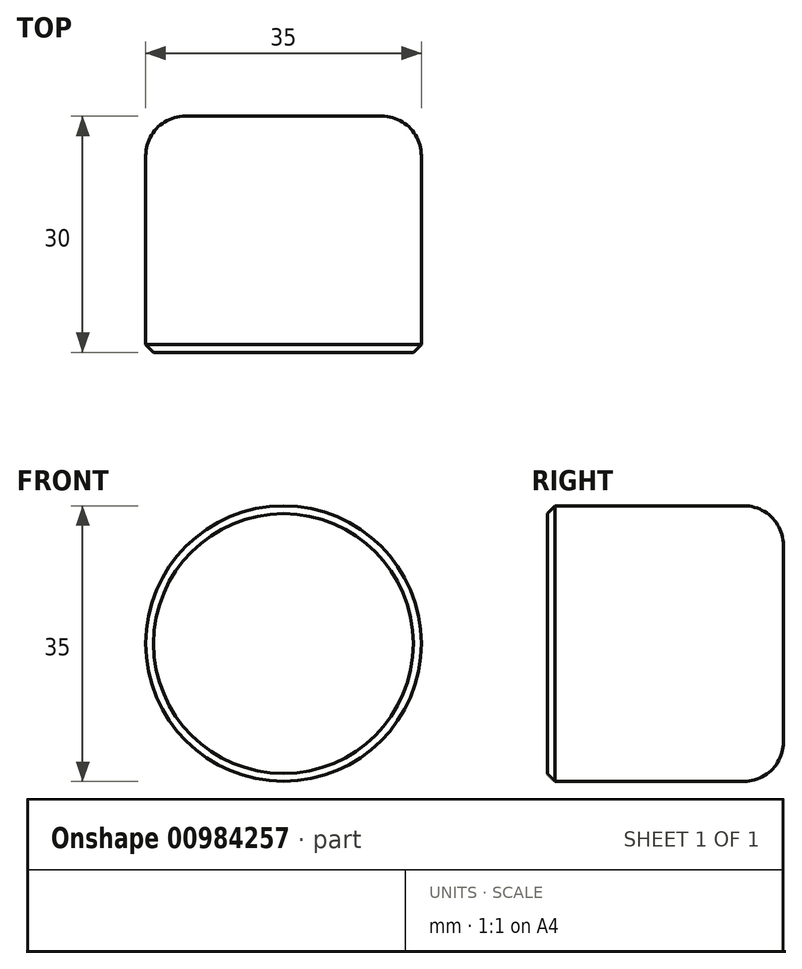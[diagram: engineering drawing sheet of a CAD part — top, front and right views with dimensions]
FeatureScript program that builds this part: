
annotation { "Feature Type Name" : "Feature", "Feature Type Description" : "" }
export const myFeature = defineFeature(function(context is Context, id is Id, definition is map)
    precondition{}
    {
        {
            var Q0;
            Q0=qCreatedBy(makeId("Front.planeOp"),FACE);
            var sketch = newSketch(context, id + "F0", { "sketchPlane" : qUnion([Q0])});
            skCircle(sketch, "E0", {"center": v(0, 0) * mm, "radius": 17.5 * mm});
            skSolve(sketch);
        }
        {
            var Q0;
            Q0=makeQuery(id+"F0.imprint","IMPRINT",FACE,{"disambiguationData":[TD([[makeQuery(id+"F0.imprint","IMPRINT",EDGE,{"derivedFrom":sQuery(id+"F0.wireOp",EDGE,"E0")}),1.0]])]});
            extrude(context, id + "F1", {"entities" : qUnion([Q0]), "depth" : 30 * mm, "offsetDistance" : 25 * mm});
        }
        {
            var Q0;
            Q0=makeQuery(id+"F1.opExtrude","CAP_EDGE",EDGE,{"disambiguationData":[OSD([sQuery(id+"F0.wireOp",EDGE,"E0")])],"isStart":true});
            fillet(context, id + "F2", {"entities" : qUnion([Q0]), "radius" : 5 * mm, "tangentPropagation" : true, "allowEdgeOverflow" : false});
        }
        {
            var Q0;
            Q0=makeQuery(id+"F1.opExtrude","CAP_EDGE",EDGE,{"disambiguationData":[OSD([sQuery(id+"F0.wireOp",EDGE,"E0")])],"isStart":false});
            chamfer(context, id + "F3", {"entities" : qUnion([Q0]), "width" : 1 * mm, "tangentPropagation" : true});
        }
    });
